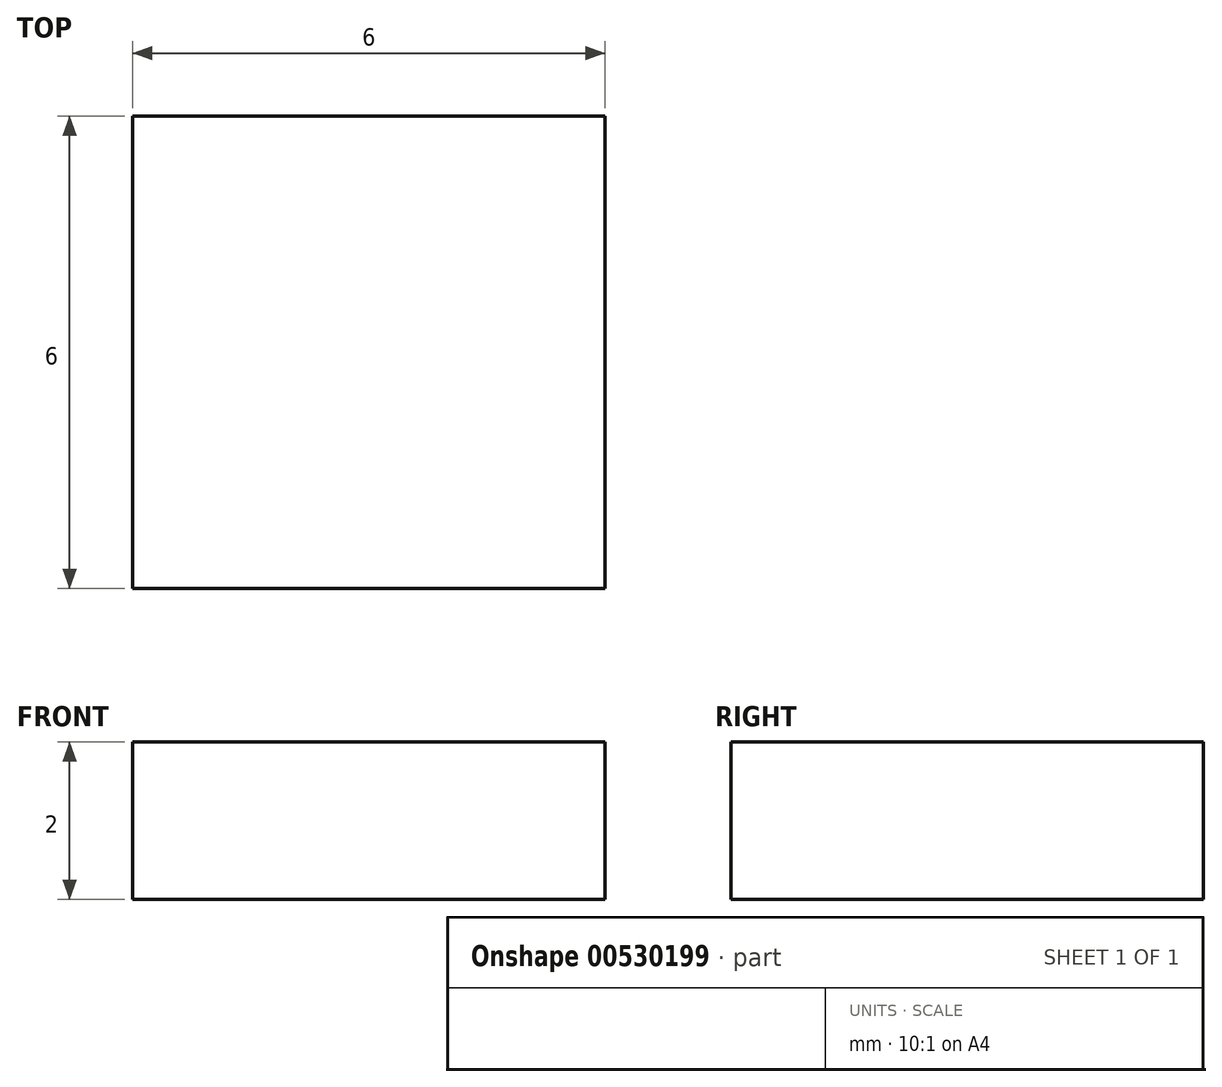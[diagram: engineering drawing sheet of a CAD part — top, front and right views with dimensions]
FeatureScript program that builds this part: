
annotation { "Feature Type Name" : "Feature", "Feature Type Description" : "" }
export const myFeature = defineFeature(function(context is Context, id is Id, definition is map)
    precondition{}
    {
        {
            var Q0;
            Q0=qCreatedBy(makeId("Top.planeOp"),FACE);
            var sketch = newSketch(context, id + "F0", { "sketchPlane" : qUnion([Q0])});
            skLineSegment(sketch, "E0.bottom", {"start": v(3, 3) * mm, "end": v(-3, 3) * mm});
            skLineSegment(sketch, "E0.top", {"start": v(3, -3) * mm, "end": v(-3, -3) * mm});
            skLineSegment(sketch, "E0.left", {"start": v(3, 3) * mm, "end": v(3, -3) * mm});
            skLineSegment(sketch, "E0.right", {"start": v(-3, 3) * mm, "end": v(-3, -3) * mm});
            skPoint(sketch, "E0.middle", {"position": v(0, 0) * mm});
            skSolve(sketch);
        }
        {
            var Q0;
            Q0=makeQuery(id+"F0.imprint","IMPRINT",FACE,{"disambiguationData":[TD([[makeQuery(id+"F0.imprint","IMPRINT",EDGE,{"derivedFrom":sQuery(id+"F0.wireOp",EDGE,"E0.bottom")}),1.0]])]});
            extrude(context, id + "F1", {"entities" : qUnion([Q0]), "depth" : 2 * mm, "offsetDistance" : 25.4 * mm});
        }
    });
